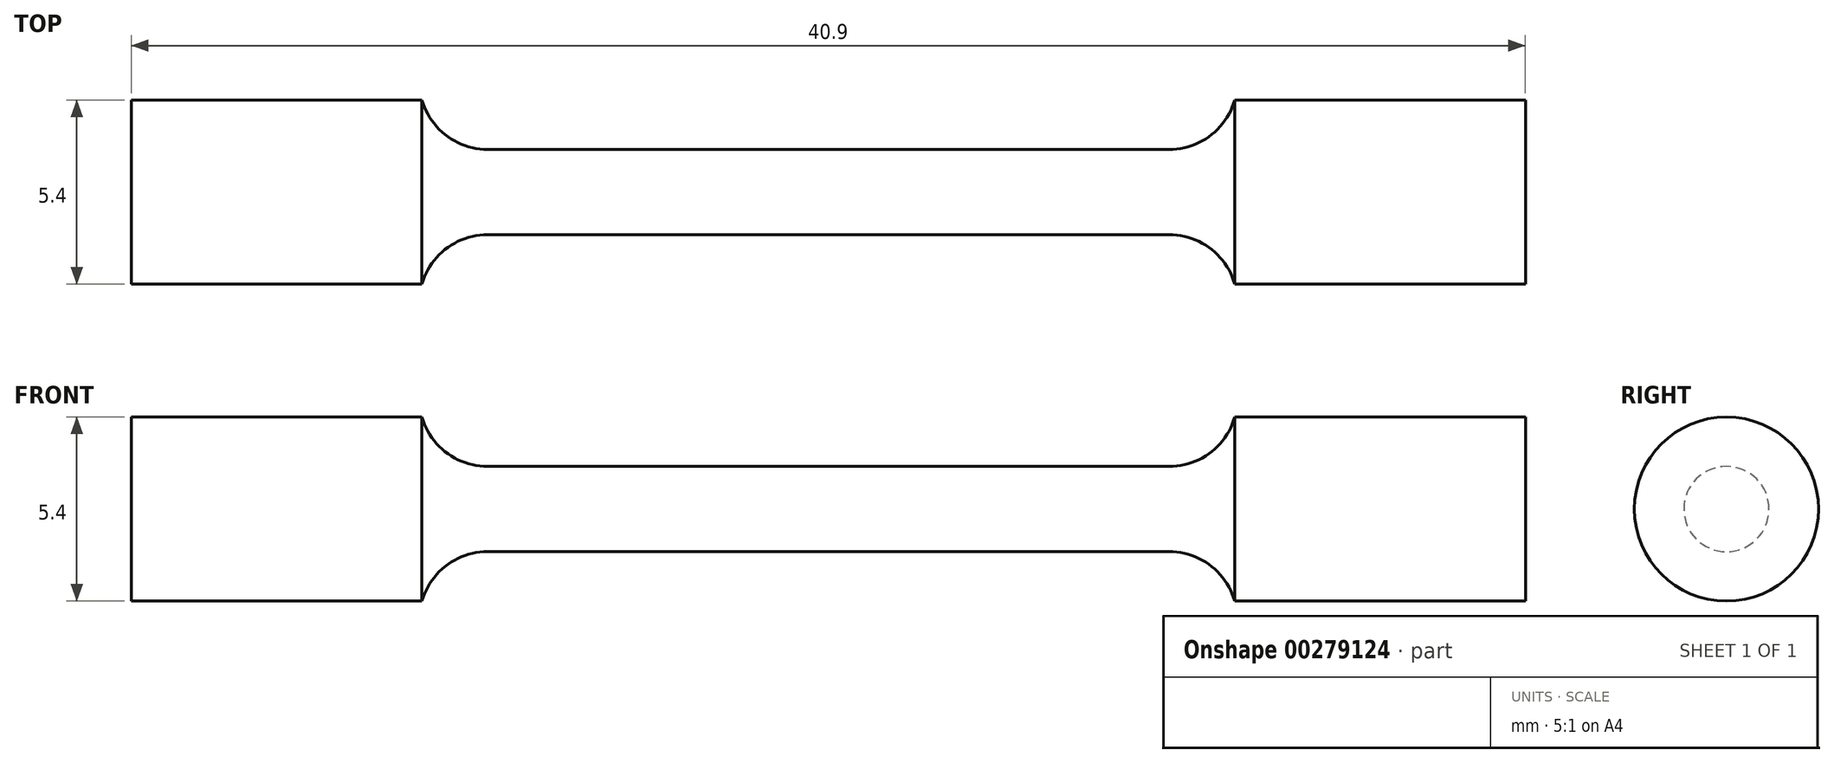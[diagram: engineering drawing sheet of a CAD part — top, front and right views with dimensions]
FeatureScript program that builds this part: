
annotation { "Feature Type Name" : "Feature", "Feature Type Description" : "" }
export const myFeature = defineFeature(function(context is Context, id is Id, definition is map)
    precondition{}
    {
        {
            var Q0;
            Q0=qCreatedBy(makeId("Front.planeOp"),FACE);
            var sketch = newSketch(context, id + "F0", { "sketchPlane" : qUnion([Q0])});
            skLineSegment(sketch, "E0", {"start": v(0, 1.25) * mm, "end": v(10, 1.25) * mm});
            skArc(sketch, "E1", {"start": v(10, 1.25) * mm, "mid": v(11.2, 1.65) * mm, "end": v(11.92, 2.7) * mm});
            skLineSegment(sketch, "E2", {"start": v(11.92, 2.7) * mm, "end": v(20.45, 2.7) * mm});
            skLineSegment(sketch, "E3", {"start": v(20.45, 2.7) * mm, "end": v(20.45, 0) * mm});
            skLineSegment(sketch, "E4", {"start": v(20.45, 0) * mm, "end": v(0, 0) * mm});
            skLineSegment(sketch, "E5.MirrorCS", {"start": v(0, 1.25) * mm, "end": v(-10, 1.25) * mm});
            skLineSegment(sketch, "E6.MirrorCS", {"start": v(-20.45, 0) * mm, "end": v(0, 0) * mm});
            skLineSegment(sketch, "E7.MirrorCS", {"start": v(-11.92, 2.7) * mm, "end": v(-20.45, 2.7) * mm});
            skLineSegment(sketch, "E8.MirrorCS", {"start": v(-20.45, 2.7) * mm, "end": v(-20.45, 0) * mm});
            skArc(sketch, "E9.MirrorCS", {"start": v(-10, 1.25) * mm, "mid": v(-11.2, 1.65) * mm, "end": v(-11.92, 2.7) * mm});
            skSolve(sketch);
        }
        {
            var Q0;
            Q0 = qSketchRegion(id + "F0", true);
            var Q1;
            Q1=sQuery(id+"F0.wireOp",EDGE,"E6.MirrorCS");
            revolve(context, id + "F1", {"entities" : qUnion([Q0]), "axis" : qUnion([Q1]), "revolveType" : RevolveType.FULL});
        }
    });
